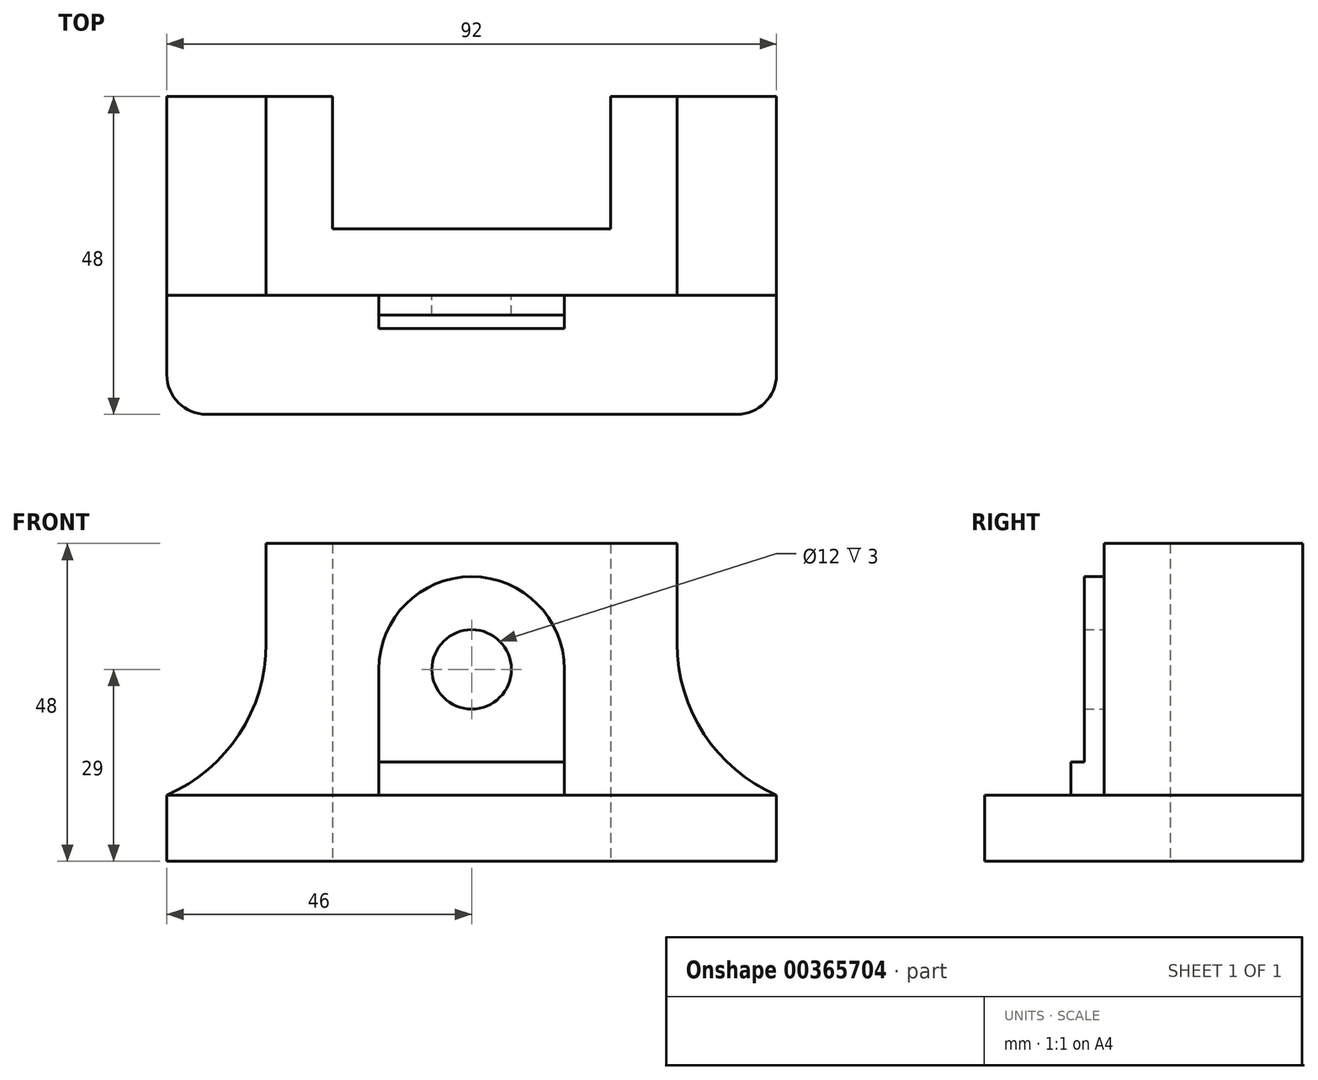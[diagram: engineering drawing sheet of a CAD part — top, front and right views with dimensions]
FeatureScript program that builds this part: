
annotation { "Feature Type Name" : "Feature", "Feature Type Description" : "" }
export const myFeature = defineFeature(function(context is Context, id is Id, definition is map)
    precondition{}
    {
        {
            var Q0;
            Q0=qCreatedBy(makeId("Top.planeOp"),FACE);
            var sketch = newSketch(context, id + "F0", { "sketchPlane" : qUnion([Q0])});
            skPoint(sketch, "E0.middle", {"position": v(0, 0) * mm});
            skLineSegment(sketch, "E1", {"start": v(0, 10) * mm, "end": v(-21, 10) * mm});
            skLineSegment(sketch, "E2", {"start": v(-21, 10) * mm, "end": v(-21, 30) * mm});
            skLineSegment(sketch, "E3", {"start": v(-21, 30) * mm, "end": v(-46, 30) * mm});
            skLineSegment(sketch, "E4", {"start": v(-46, 30) * mm, "end": v(-46, -18) * mm});
            skLineSegment(sketch, "E5", {"start": v(-46, -18) * mm, "end": v(46, -18) * mm});
            skLineSegment(sketch, "E6", {"start": v(46, -18) * mm, "end": v(46, 30) * mm});
            skLineSegment(sketch, "E7", {"start": v(46, 30) * mm, "end": v(21, 30) * mm});
            skLineSegment(sketch, "E8", {"start": v(21, 30) * mm, "end": v(21, 10) * mm});
            skLineSegment(sketch, "E9", {"start": v(21, 10) * mm, "end": v(0, 10) * mm});
            skLineSegment(sketch, "E10", {"start": v(31, 0) * mm, "end": v(-31, 0) * mm});
            skLineSegment(sketch, "E11", {"start": v(-31, 0) * mm, "end": v(-31, 30) * mm});
            skLineSegment(sketch, "E12", {"start": v(31, 0) * mm, "end": v(31, 30) * mm});
            skLineSegment(sketch, "E13", {"start": v(31, 0) * mm, "end": v(46, 0) * mm});
            skLineSegment(sketch, "E14", {"start": v(-31, 0) * mm, "end": v(-46, 0) * mm});
            skSolve(sketch);
        }
        {
            var Q0;
            Q0=makeQuery(id+"F0.imprint","IMPRINT",FACE,{"disambiguationData":[TD([[makeQuery(id+"F0.imprint","IMPRINT",EDGE,{"derivedFrom":sQuery(id+"F0.wireOp",EDGE,"E1")}),1.0]])]});
            var Q1;
            {var subQ4=sQuery(id+"F0.wireOp",EDGE,"E12");Q1=makeQuery(id+"F0.imprint","IMPRINT",FACE,{"disambiguationData":[TD([[makeQuery(id+"F0.imprint","IMPRINT",EDGE,{"derivedFrom":subQ4}),-1.0]])]});}
            var Q2;
            {var subQ3=sQuery(id+"F0.wireOp",EDGE,"E11");Q2=makeQuery(id+"F0.imprint","IMPRINT",FACE,{"disambiguationData":[TD([[makeQuery(id+"F0.imprint","IMPRINT",EDGE,{"derivedFrom":subQ3}),1.0]])]});}
            extrude(context, id + "F1", {"entities" : qUnion([Q0, Q1, Q2]), "depth" : 48 * mm});
        }
        {
            var Q0;
            {var subQ1=sQuery(id+"F0.wireOp",EDGE,"E5");Q0=makeQuery(id+"F0.imprint","IMPRINT",FACE,{"disambiguationData":[TD([[makeQuery(id+"F0.imprint","IMPRINT",EDGE,{"derivedFrom":subQ1}),1.0]])]});}
            extrude(context, id + "F2", {"entities" : qUnion([Q0]), "operationType" : NewBodyOperationType.ADD, "depth" : 10 * mm});
        }
        {
            var Q0;
            Q0=makeQuery(id+"F1.opExtrude","CAP_FACE",FACE,{"disambiguationData":[OSD([sQuery(id+"F0.wireOp",EDGE,"E1"),sQuery(id+"F0.wireOp",EDGE,"E2"),sQuery(id+"F0.wireOp",EDGE,"E3"),sQuery(id+"F0.wireOp",EDGE,"E4"),sQuery(id+"F0.wireOp",EDGE,"E6"),sQuery(id+"F0.wireOp",EDGE,"E7"),sQuery(id+"F0.wireOp",EDGE,"E8"),sQuery(id+"F0.wireOp",EDGE,"E9"),sQuery(id+"F0.wireOp",EDGE,"E10"),sQuery(id+"F0.wireOp",EDGE,"E13"),sQuery(id+"F0.wireOp",EDGE,"E14")])],"isStart":false});
            var sketch = newSketch(context, id + "F3", { "sketchPlane" : qUnion([Q0])});
            skLineSegment(sketch, "E15", {"start": v(31, 30) * mm, "end": v(31, 0) * mm});
            skLineSegment(sketch, "E16", {"start": v(31, 0) * mm, "end": v(46, 0) * mm});
            skLineSegment(sketch, "E17", {"start": v(46, 0) * mm, "end": v(46, 30) * mm});
            skLineSegment(sketch, "E18", {"start": v(46, 30) * mm, "end": v(31, 30) * mm});
            skLineSegment(sketch, "E19.MirrorCS", {"start": v(-46, 30) * mm, "end": v(-31, 30) * mm});
            skLineSegment(sketch, "E20.MirrorCS", {"start": v(-31, 30) * mm, "end": v(-31, 0) * mm});
            skLineSegment(sketch, "E21.MirrorCS", {"start": v(-31, 0) * mm, "end": v(-46, 0) * mm});
            skLineSegment(sketch, "E22.MirrorCS", {"start": v(-46, 0) * mm, "end": v(-46, 30) * mm});
            skSolve(sketch);
        }
        {
            var Q0;
            Q0=makeQuery(id+"F3.imprint","IMPRINT",FACE,{"disambiguationData":[TD([[makeQuery(id+"F3.imprint","IMPRINT",EDGE,{"derivedFrom":sQuery(id+"F3.wireOp",EDGE,"E19.MirrorCS")}),1.0]])]});
            var Q1;
            Q1=makeQuery(id+"F3.imprint","IMPRINT",FACE,{"disambiguationData":[TD([[makeQuery(id+"F3.imprint","IMPRINT",EDGE,{"derivedFrom":sQuery(id+"F3.wireOp",EDGE,"E15")}),1.0]])]});
            extrude(context, id + "F4", {"entities" : qUnion([Q0, Q1]), "operationType" : NewBodyOperationType.REMOVE, "oppositeDirection" : true, "depth" : 38 * mm});
        }
        {
            var Q0;
            Q0=makeQuery(id+"F4.boolean.opBoolean","COPY",EDGE,{"derivedFrom":makeQuery(id+"F4.opExtrude","CAP_EDGE",EDGE,{"disambiguationData":[OSD([sQuery(id+"F3.wireOp",EDGE,"E15")])],"isStart":false})});
            var Q1;
            Q1=makeQuery(id+"F4.boolean.opBoolean","COPY",EDGE,{"derivedFrom":makeQuery(id+"F4.opExtrude","CAP_EDGE",EDGE,{"disambiguationData":[OSD([sQuery(id+"F3.wireOp",EDGE,"E20.MirrorCS")])],"isStart":false})});
            fillet(context, id + "F5", {"entities" : qUnion([Q0, Q1]), "radius" : 25 * mm, "tangentPropagation" : true, "allowEdgeOverflow" : false});
        }
        {
            var Q0;
            Q0=makeQuery(id+"F1.opExtrude","SWEPT_FACE",FACE,{"disambiguationData":[OSD([sQuery(id+"F0.wireOp",EDGE,"E10"),sQuery(id+"F0.wireOp",EDGE,"E13"),sQuery(id+"F0.wireOp",EDGE,"E14")])]});
            var sketch = newSketch(context, id + "F6", { "sketchPlane" : qUnion([Q0])});
            skLineSegment(sketch, "E23", {"start": v(-14, 10) * mm, "end": v(-14, 29) * mm});
            skLineSegment(sketch, "E24", {"start": v(-14, 29) * mm, "end": v(14, 29) * mm});
            skLineSegment(sketch, "E25", {"start": v(14, 29) * mm, "end": v(14, 10) * mm});
            skLineSegment(sketch, "E26", {"start": v(14, 10) * mm, "end": v(-14, 10) * mm});
            skArc(sketch, "E27", {"start": v(14, 29) * mm, "mid": v(0, 43) * mm, "end": v(-14, 29) * mm});
            skCircle(sketch, "E28", {"center": v(0, 29) * mm, "radius": 6 * mm});
            skSolve(sketch);
        }
        {
            var Q0;
            {var subQ5=sQuery(id+"F6.wireOp",EDGE,"E23");Q0=makeQuery(id+"F6.imprint","IMPRINT",FACE,{"disambiguationData":[TD([[makeQuery(id+"F6.imprint","IMPRINT",EDGE,{"derivedFrom":subQ5}),-1.0]])]});}
            var Q1;
            {var subQ0=sQuery(id+"F6.wireOp",EDGE,"E27");Q1=makeQuery(id+"F6.imprint","IMPRINT",FACE,{"disambiguationData":[TD([[makeQuery(id+"F6.imprint","IMPRINT",EDGE,{"derivedFrom":subQ0}),1.0]])]});}
            extrude(context, id + "F7", {"entities" : qUnion([Q0, Q1]), "operationType" : NewBodyOperationType.ADD, "depth" : 3 * mm});
        }
        {
            var Q0;
            Q0=makeQuery(id+"F7.opExtrude","CAP_FACE",FACE,{"disambiguationData":[OSD([sQuery(id+"F6.wireOp",EDGE,"E23"),sQuery(id+"F6.wireOp",EDGE,"E25"),sQuery(id+"F6.wireOp",EDGE,"E26"),sQuery(id+"F6.wireOp",EDGE,"E27"),sQuery(id+"F6.wireOp",EDGE,"E28")])],"isStart":false});
            var sketch = newSketch(context, id + "F8", { "sketchPlane" : qUnion([Q0])});
            skLineSegment(sketch, "E29", {"start": v(-14, 15) * mm, "end": v(14, 15) * mm});
            skSolve(sketch);
        }
        {
            var Q0;
            {var subQ0=sQuery(id+"F8.wireOp",EDGE,"E29");Q0=makeQuery(id+"F8.imprint","IMPRINT",FACE,{"disambiguationData":[TD([[makeQuery(id+"F8.imprint","IMPRINT",EDGE,{"derivedFrom":subQ0}),-1.0]])]});}
            extrude(context, id + "F9", {"entities" : qUnion([Q0]), "operationType" : NewBodyOperationType.ADD, "depth" : 2 * mm});
        }
        {
            var Q0;
            Q0=makeQuery(id+"F2.opExtrude","SWEPT_EDGE",EDGE,{"disambiguationData":[OSD([sQuery(id+"F0.wireOp",EDGE,"E5"),sQuery(id+"F0.wireOp",EDGE,"E6")])]});
            var Q1;
            Q1=makeQuery(id+"F2.opExtrude","SWEPT_EDGE",EDGE,{"disambiguationData":[OSD([sQuery(id+"F0.wireOp",EDGE,"E4"),sQuery(id+"F0.wireOp",EDGE,"E5")])]});
            fillet(context, id + "F10", {"entities" : qUnion([Q0, Q1]), "radius" : 6 * mm, "tangentPropagation" : true, "allowEdgeOverflow" : false});
        }
    });
